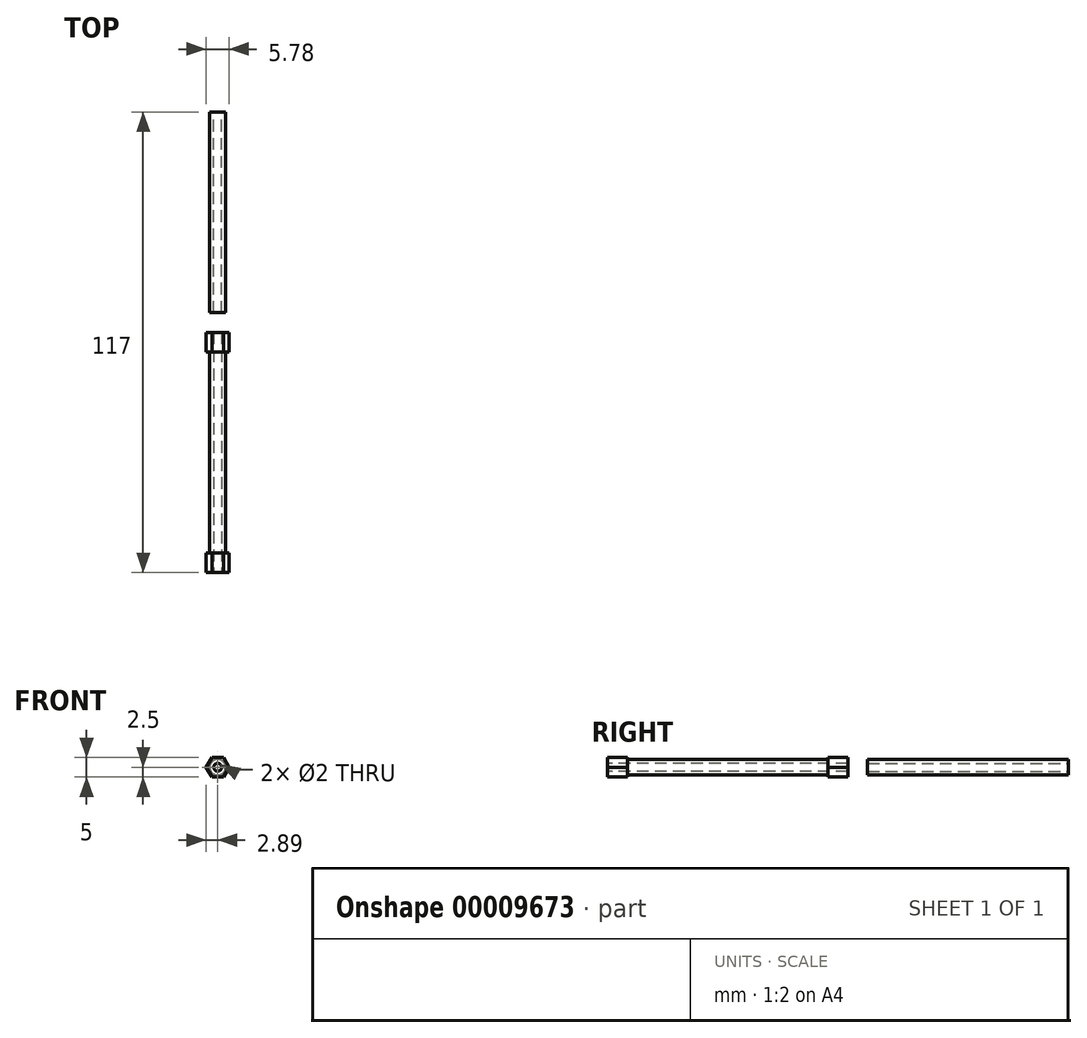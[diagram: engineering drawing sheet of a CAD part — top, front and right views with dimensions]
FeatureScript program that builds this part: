
annotation { "Feature Type Name" : "Feature", "Feature Type Description" : "" }
export const myFeature = defineFeature(function(context is Context, id is Id, definition is map)
    precondition{}
    {
        {
            var Q0;
            Q0=qCreatedBy(makeId("Front.planeOp"),FACE);
            cPlane(context, id + "F0", {"entities" : qUnion([Q0]), "cplaneType" : CPlaneType.OFFSET, "offset" : 30.5 * mm, "width" : 150 * mm, "height" : 150 * mm});
        }
        {
            var Q0;
            Q0=qCreatedBy(makeId("Front.planeOp"),FACE);
            var sketch = newSketch(context, id + "F1", { "sketchPlane" : qUnion([Q0])});
            skCircle(sketch, "E0.cCircle", {"center": v(0, 0) * mm, "radius": 2.5 * mm, "construction": true});
            skLineSegment(sketch, "E0.0", {"start": v(-1.44, 2.5) * mm, "end": v(1.44, 2.5) * mm});
            skLineSegment(sketch, "E0.1", {"start": v(1.44, 2.5) * mm, "end": v(2.89, 0) * mm});
            skLineSegment(sketch, "E0.2", {"start": v(2.89, 0) * mm, "end": v(1.44, -2.5) * mm});
            skLineSegment(sketch, "E0.3", {"start": v(1.44, -2.5) * mm, "end": v(-1.44, -2.5) * mm});
            skLineSegment(sketch, "E0.4", {"start": v(-1.44, -2.5) * mm, "end": v(-2.89, 0) * mm});
            skLineSegment(sketch, "E0.5", {"start": v(-2.89, 0) * mm, "end": v(-1.44, 2.5) * mm});
            skPoint(sketch, "E0.0.midPoint", {"position": v(0, 2.5) * mm});
            skSolve(sketch);
        }
        {
            var Q0;
            Q0 = qSketchRegion(id + "F1", true);
            extrude(context, id + "F2", {"entities" : qUnion([Q0]), "depth" : 5 * mm});
        }
        {
            var Q0;
            Q0=makeQuery(id+"F2.opExtrude","SWEPT_BODY",BODY,{"disambiguationData":[OSD([sQuery(id+"F1.wireOp",EDGE,"E0.0"),sQuery(id+"F1.wireOp",EDGE,"E0.1"),sQuery(id+"F1.wireOp",EDGE,"E0.2"),sQuery(id+"F1.wireOp",EDGE,"E0.3"),sQuery(id+"F1.wireOp",EDGE,"E0.4"),sQuery(id+"F1.wireOp",EDGE,"E0.5")])]});
            var Q1;
            Q1=qCreatedBy(id+"F0.planeOp",FACE);
            mirror(context, id + "F3", {"entities" : qUnion([Q0]), "mirrorPlane" : qUnion([Q1])});
        }
        {
            var Q0;
            Q0=makeQuery(id+"F2.opExtrude","CAP_FACE",FACE,{"disambiguationData":[OSD([sQuery(id+"F1.wireOp",EDGE,"E0.0"),sQuery(id+"F1.wireOp",EDGE,"E0.1"),sQuery(id+"F1.wireOp",EDGE,"E0.2"),sQuery(id+"F1.wireOp",EDGE,"E0.3"),sQuery(id+"F1.wireOp",EDGE,"E0.4"),sQuery(id+"F1.wireOp",EDGE,"E0.5")])],"isStart":false});
            var sketch = newSketch(context, id + "F4", { "sketchPlane" : qUnion([Q0])});
            skCircle(sketch, "E1", {"center": v(0, 0) * mm, "radius": 2 * mm});
            skSolve(sketch);
        }
        {
            var Q0;
            Q0=makeQuery(id+"F3.opPattern","COPY",FACE,{"derivedFrom":makeQuery(id+"F2.opExtrude","CAP_FACE",FACE,{"disambiguationData":[OSD([sQuery(id+"F1.wireOp",EDGE,"E0.0"),sQuery(id+"F1.wireOp",EDGE,"E0.1"),sQuery(id+"F1.wireOp",EDGE,"E0.2"),sQuery(id+"F1.wireOp",EDGE,"E0.3"),sQuery(id+"F1.wireOp",EDGE,"E0.4"),sQuery(id+"F1.wireOp",EDGE,"E0.5")])],"isStart":false}),"instanceName":"1"});
            var sketch = newSketch(context, id + "F5", { "sketchPlane" : qUnion([Q0])});
            skCircle(sketch, "E2", {"center": v(0, 0) * mm, "radius": 2 * mm});
            skSolve(sketch);
        }
        {
            var Q0;
            Q0=makeQuery(id+"F4.imprint","IMPRINT",FACE,{"disambiguationData":[TD([[makeQuery(id+"F4.imprint","IMPRINT",EDGE,{"derivedFrom":sQuery(id+"F4.wireOp",EDGE,"E1")}),1.0]])]});
            var Q1;
            Q1=makeQuery(id+"F5.imprint","IMPRINT",FACE,{"disambiguationData":[TD([[makeQuery(id+"F5.imprint","IMPRINT",EDGE,{"derivedFrom":sQuery(id+"F5.wireOp",EDGE,"E2")}),1.0]])]});
            loft(context, id + "F6", {"sheetProfilesArray" : [{ "sheetProfileEntities" : qUnion([Q0]) }, { "sheetProfileEntities" : qUnion([Q1]) }]});
        }
        {
            var Q0;
            Q0=makeQuery(id+"F3.opPattern","COPY",FACE,{"derivedFrom":makeQuery(id+"F2.opExtrude","CAP_FACE",FACE,{"disambiguationData":[OSD([sQuery(id+"F1.wireOp",EDGE,"E0.0"),sQuery(id+"F1.wireOp",EDGE,"E0.1"),sQuery(id+"F1.wireOp",EDGE,"E0.2"),sQuery(id+"F1.wireOp",EDGE,"E0.3"),sQuery(id+"F1.wireOp",EDGE,"E0.4"),sQuery(id+"F1.wireOp",EDGE,"E0.5")])],"isStart":true}),"instanceName":"1"});
            var sketch = newSketch(context, id + "F7", { "sketchPlane" : qUnion([Q0])});
            skCircle(sketch, "E3", {"center": v(0, 0) * mm, "radius": 1 * mm});
            skSolve(sketch);
        }
        {
            var Q0;
            Q0=makeQuery(id+"F7.imprint","IMPRINT",FACE,{"disambiguationData":[TD([[makeQuery(id+"F7.imprint","IMPRINT",EDGE,{"derivedFrom":sQuery(id+"F7.wireOp",EDGE,"E3")}),1.0]])]});
            extrude(context, id + "F8", {"entities" : qUnion([Q0]), "operationType" : NewBodyOperationType.REMOVE, "oppositeDirection" : true, "depth" : 72 * mm});
        }
        {
            var Q0;
            Q0=makeQuery(id+"F6.opLoft","SWEPT_BODY",BODY,{"disambiguationData":[OSD([makeQuery(id+"F4.imprint","IMPRINT",FACE,{"disambiguationData":[TD([[makeQuery(id+"F4.imprint","IMPRINT",EDGE,{"derivedFrom":sQuery(id+"F4.wireOp",EDGE,"E1")}),1.0]])]}),makeQuery(id+"F5.imprint","IMPRINT",FACE,{"disambiguationData":[TD([[makeQuery(id+"F5.imprint","IMPRINT",EDGE,{"derivedFrom":sQuery(id+"F5.wireOp",EDGE,"E2")}),1.0]])]})])]});
            var Q1;
            Q1=makeQuery(id+"F2.opExtrude","CAP_FACE",FACE,{"disambiguationData":[OSD([sQuery(id+"F1.wireOp",EDGE,"E0.0"),sQuery(id+"F1.wireOp",EDGE,"E0.1"),sQuery(id+"F1.wireOp",EDGE,"E0.2"),sQuery(id+"F1.wireOp",EDGE,"E0.3"),sQuery(id+"F1.wireOp",EDGE,"E0.4"),sQuery(id+"F1.wireOp",EDGE,"E0.5")])],"isStart":true});
            mirror(context, id + "F9", {"operationType" : NewBodyOperationType.ADD, "entities" : qUnion([Q0]), "mirrorPlane" : qUnion([Q1])});
        }
    });
